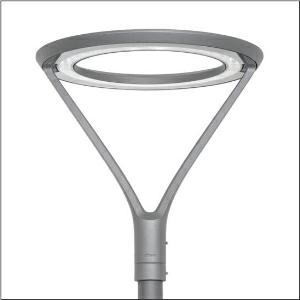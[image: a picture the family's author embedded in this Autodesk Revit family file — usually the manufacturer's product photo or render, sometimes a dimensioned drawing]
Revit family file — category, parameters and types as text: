
# Revit family: dl_r__20___pl1_2s_5xa51283ws008_843d
name_source: partatom
category: Lighting Fixtures
units: mm (PartAtom-declared; Revit-internal decimal feet)

## family parameters
Cut with Voids When Loaded = No
Host = Face
Light Source = No
Part Type = Normal
Room Calculation Point = No
Round Connector Dimension = Use Diameter
Shared = No

## types (1)
- --- (1 x LED, 3080 lm, 24.6 W, 3000K)
    Apparent Load = 25 VA
    CIE Flux Codes = 33 78 99 100 100
    Color Rendering = 70
    Color Temperature = 3000K
    Default Elevation = 1800 mm
    Description = DL® 20, mast luminaire, primary light control with reflector, highly specular, primary optical cover: cover, of toughened safety glass of clear glass with excellent transmission level, light distribution: PL1.2s, light emission: direct distribution, primary light characteristic: symmetric, installation type: post-top, LED, High Power LED, rated luminous flux: 3.040lm, luminous efficacy: 86lm/W, light colour: 730, colour temperature: 3000K, control gear: ECG Plus, control: overheat protection, power reduction, digital communication interface, constant luminous flux control, time-dependent luminous flux control, flexible luminous flux parameterisation, electronic power reduction, mains connection: 230..240V, 50/60Hz, connection cable pre-assembled, cable length: 5m, start of lifetime: 36W, end of service life: 36W, reduction: 17W, luminaire housing, upper part, of cast aluminium, powder-coated, Siteco® metallic grey (DB 702S), diameter: 690mm, height: 690mm, spigot size: 76mm (post-top), luminaire housing, of cast aluminium, powder-coated, Siteco® metallic grey (DB 702S), equipment: standard, protection rating (complete): IP66, insulation class (complete): insulation class II (safety insulation), certification: CE, ENEC, VDE, impact resistance: IK08, permissible operating ambient temperature: -25..+35°C, standard-compliant lighting for roads and squares, packaging unit: 1 piece

Light Distribution: PL1.2s
    Height = 690 mm
    Lamp = 1 x LED
    Lamp Light Flux = 3080 lm
    Lamp Power = 24.6 W
    Lamp count = 1
    Length = 690 mm
    Luminous efficacy = 125 lm/W
    Manufacturer = Siteco
    ModVariant = No
    Model = 5XA51283WS008
    Number of Poles = 1
    OnlyDefault = Yes
    Power Factor = 1
    Product Name = DL® 20 | PL1.2s
    Product group = mast luminaire | pylon top
    ProductGroupID = 6100
    Protection Class = Protection class II
    Protection Degree = IP 66
    RLX_Detail_Level = 1
    RLX_Emergency_Light_Flux = 0 lm
    RLX_Emergency_Type = 0
    RLX_Emergency_Type_DB = No
    RlxData = <blob elided: 204621 chars, md5=c71c7988>
    Socket = socket
    Standby Power = 0 W
    System Light Flux = 3080 lm
    System Power = 25 W
    Type Comments = factory setting: luminous flux: 100 % | dim-lin: 254 | 330 mA
    Type Image = l_1006001.jpg
    URL = http://relux.com
    VarID = @adj_028019
    Voltage = 0 V
    Weight = 0.00 kg
    Width = 0 mm  [stored 0 ft]

note: [stored X ft] marks values corroborated as IEEE doubles in the binary element streams (Revit-internal decimal feet)

## geometry (parser evidence)
native form markers: Blend x4, Sweep x10
no freeform markers — native parametric forms only
